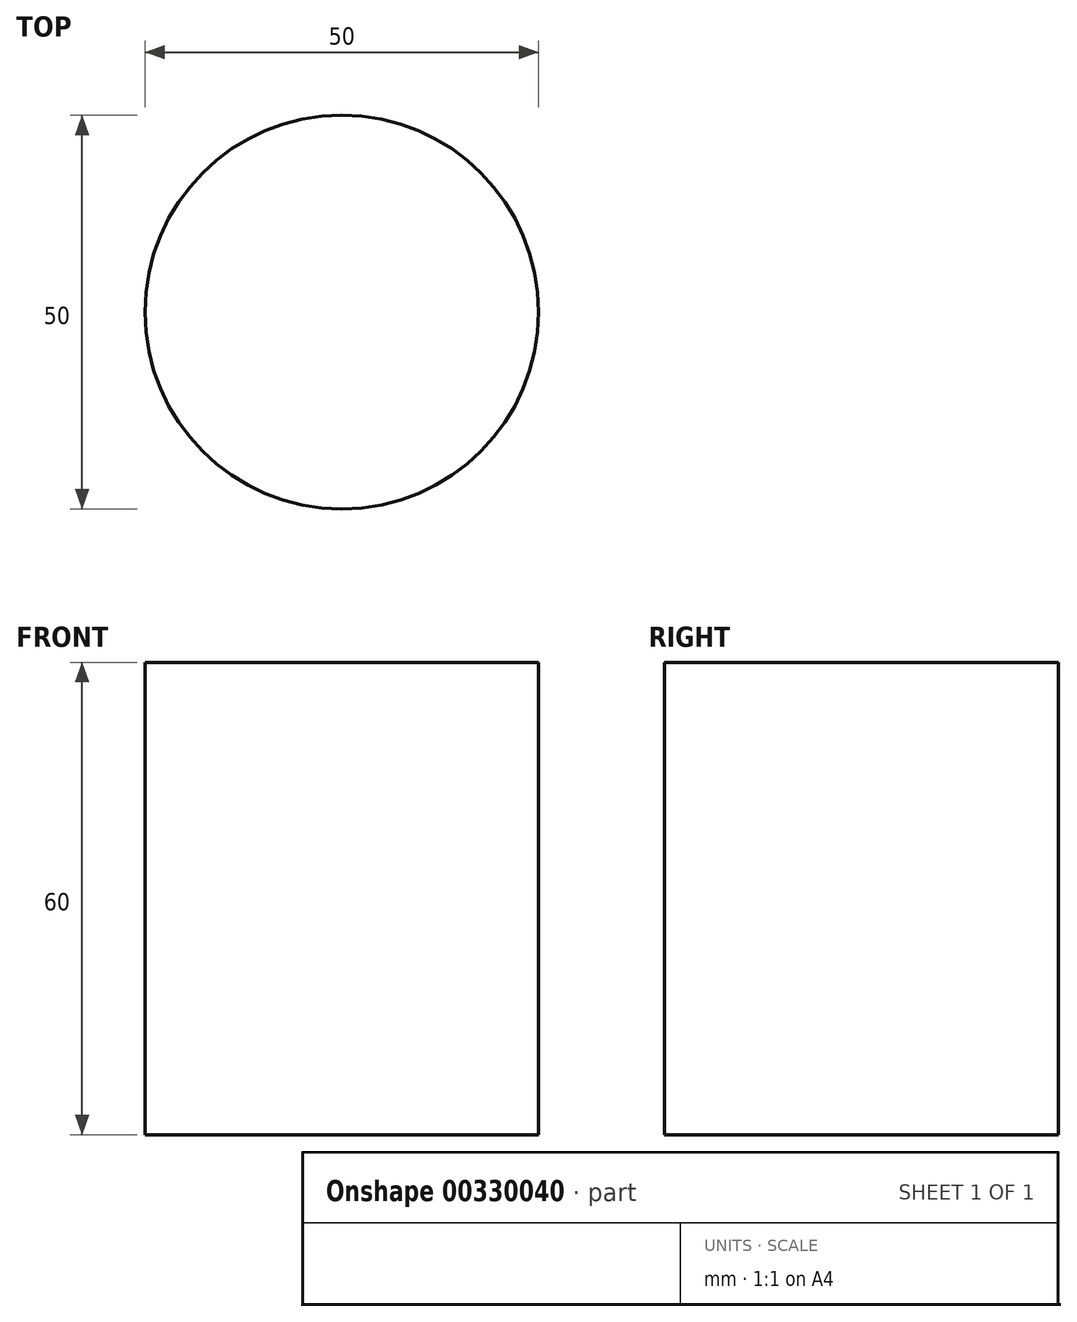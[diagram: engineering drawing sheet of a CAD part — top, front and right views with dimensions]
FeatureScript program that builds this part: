
annotation { "Feature Type Name" : "Feature", "Feature Type Description" : "" }
export const myFeature = defineFeature(function(context is Context, id is Id, definition is map)
    precondition{}
    {
        {
            var Q0;
            Q0=qCreatedBy(makeId("Top.planeOp"),FACE);
            var sketch = newSketch(context, id + "F0", { "sketchPlane" : qUnion([Q0])});
            skCircle(sketch, "E0", {"center": v(0, 0) * mm, "radius": 25 * mm});
            skSolve(sketch);
        }
        {
            var Q0;
            Q0 = qSketchRegion(id + "F0", true);
            extrude(context, id + "F1", {"entities" : qUnion([Q0]), "endBound" : BoundingType.SYMMETRIC, "depth" : 60 * mm});
        }
    });
